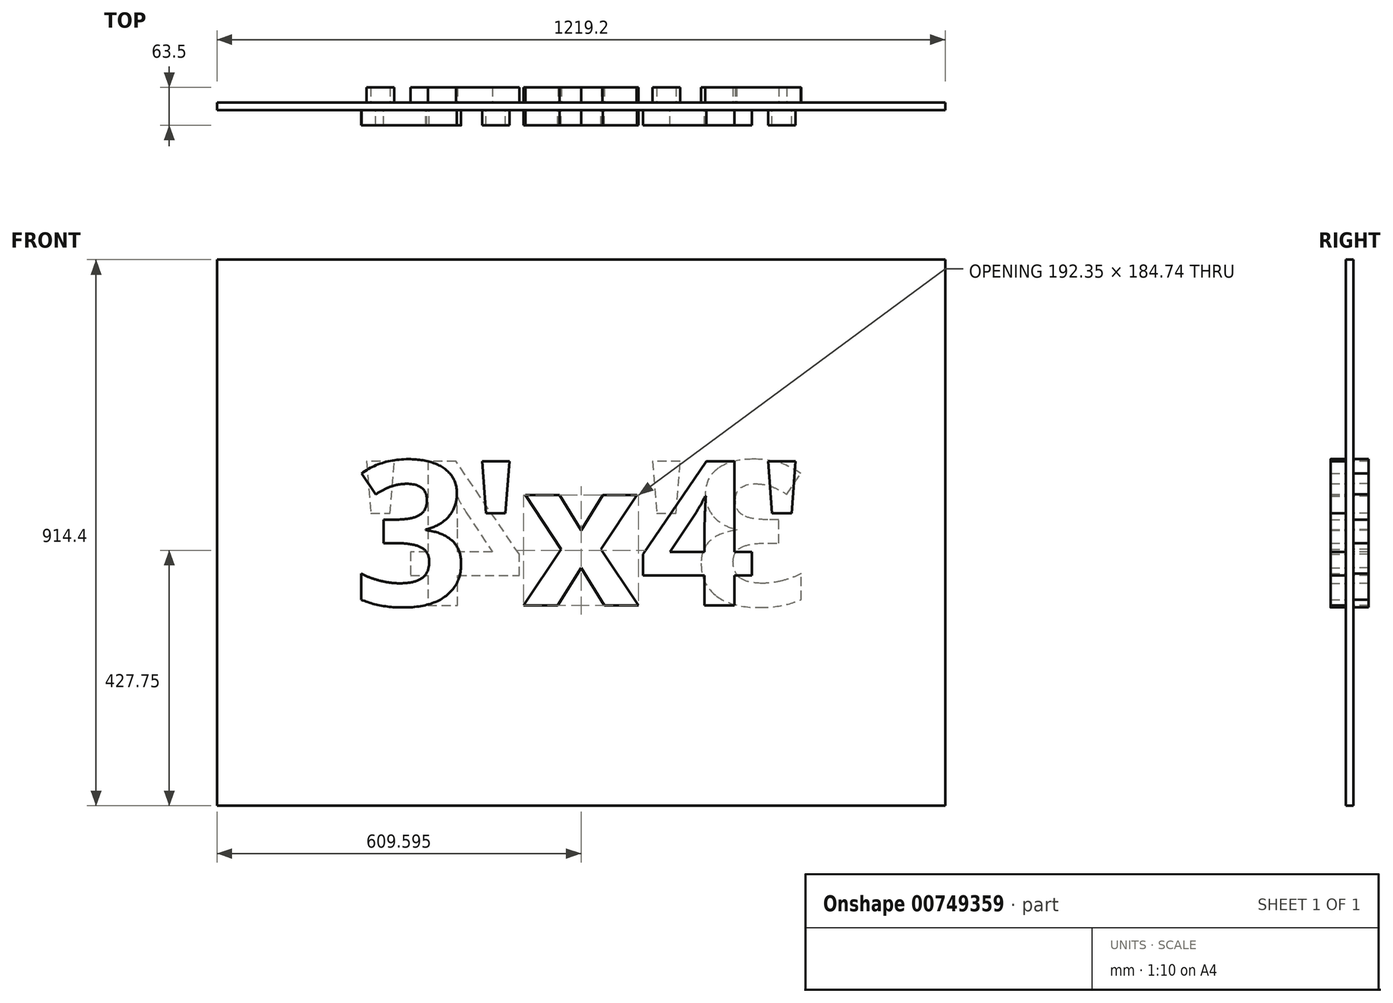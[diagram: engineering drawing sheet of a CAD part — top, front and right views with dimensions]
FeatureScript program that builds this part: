
annotation { "Feature Type Name" : "Feature", "Feature Type Description" : "" }
export const myFeature = defineFeature(function(context is Context, id is Id, definition is map)
    precondition{}
    {
        {
            var Q0;
            Q0=qCreatedBy(makeId("Front.planeOp"),FACE);
            var sketch = newSketch(context, id + "F0", { "sketchPlane" : qUnion([Q0])});
            skLineSegment(sketch, "E0.bottom", {"start": v(0, 0) * mm, "end": v(1219.2, 0) * mm});
            skLineSegment(sketch, "E0.top", {"start": v(0, 914.4) * mm, "end": v(1219.2, 914.4) * mm});
            skLineSegment(sketch, "E0.left", {"start": v(0, 0) * mm, "end": v(0, 914.4) * mm});
            skLineSegment(sketch, "E0.right", {"start": v(1219.2, 0) * mm, "end": v(1219.2, 914.4) * mm});
            skSolve(sketch);
        }
        {
            var Q0;
            Q0=makeQuery(id+"F0.imprint","IMPRINT",FACE,{"disambiguationData":[TD([[makeQuery(id+"F0.imprint","IMPRINT",EDGE,{"derivedFrom":sQuery(id+"F0.wireOp",EDGE,"E0.bottom")}),1.0]])]});
            extrude(context, id + "F1", {"entities" : qUnion([Q0]), "depth" : 12.7 * mm, "offsetDistance" : 25.4 * mm});
        }
        {
            var Q0;
            Q0=makeQuery(id+"F1.opExtrude","CAP_FACE",FACE,{"disambiguationData":[OSD([sQuery(id+"F0.wireOp",EDGE,"E0.bottom"),sQuery(id+"F0.wireOp",EDGE,"E0.top"),sQuery(id+"F0.wireOp",EDGE,"E0.left"),sQuery(id+"F0.wireOp",EDGE,"E0.right")])],"isStart":false});
            var sketch = newSketch(context, id + "F2", { "sketchPlane" : qUnion([Q0])});
            skText(sketch, "E1", { "text": "3\'x4\'", "fontName": "OpenSans-Bold.ttf"});
            skPoint(sketch, "E2", {"position": v(228.6, 457.2) * mm});
            const initialGuessF2  = {"E1": [0.2286, 0.33538, 1, 0, 0.24364]};
            skSetInitialGuess(sketch, initialGuessF2);
            skSolve(sketch);
        }
        {
            var Q0;
            Q0=makeQuery(id+"F2.imprint","IMPRINT",FACE,{"disambiguationData":[TD([[makeQuery(id+"F2.imprint","IMPRINT",EDGE,{"derivedFrom":sQuery(id+"F2.wireOp",EDGE,"E1.sketch_text.stroke-61")}),-1.0]])]});
            var Q1;
            Q1=makeQuery(id+"F2.imprint","IMPRINT",FACE,{"disambiguationData":[TD([[makeQuery(id+"F2.imprint","IMPRINT",EDGE,{"derivedFrom":sQuery(id+"F2.wireOp",EDGE,"E1.sketch_text.stroke-43")}),-1.0]])]});
            var Q2;
            Q2=makeQuery(id+"F2.imprint","IMPRINT",FACE,{"disambiguationData":[TD([[makeQuery(id+"F2.imprint","IMPRINT",EDGE,{"derivedFrom":sQuery(id+"F2.wireOp",EDGE,"E1.sketch_text.stroke-31")}),-1.0]])]});
            var Q3;
            Q3=makeQuery(id+"F2.imprint","IMPRINT",FACE,{"disambiguationData":[TD([[makeQuery(id+"F2.imprint","IMPRINT",EDGE,{"derivedFrom":sQuery(id+"F2.wireOp",EDGE,"E1.sketch_text.stroke-27")}),-1.0]])]});
            var Q4;
            Q4=makeQuery(id+"F2.imprint","IMPRINT",FACE,{"disambiguationData":[TD([[makeQuery(id+"F2.imprint","IMPRINT",EDGE,{"derivedFrom":sQuery(id+"F2.wireOp",EDGE,"E1.sketch_text.stroke-0")}),-1.0]])]});
            extrude(context, id + "F3", {"entities" : qUnion([Q0, Q1, Q2, Q3, Q4]), "operationType" : NewBodyOperationType.ADD, "depth" : 25.4 * mm, "offsetDistance" : 25.4 * mm});
        }
        {
            var Q0;
            Q0=makeQuery(id+"F1.opExtrude","CAP_FACE",FACE,{"disambiguationData":[OSD([sQuery(id+"F0.wireOp",EDGE,"E0.bottom"),sQuery(id+"F0.wireOp",EDGE,"E0.top"),sQuery(id+"F0.wireOp",EDGE,"E0.left"),sQuery(id+"F0.wireOp",EDGE,"E0.right")])],"isStart":true});
            var sketch = newSketch(context, id + "F4", { "sketchPlane" : qUnion([Q0])});
            skText(sketch, "E3", { "text": "3\'x4\'", "fontName": "OpenSans-Bold.ttf"});
            skPoint(sketch, "E4", {"position": v(-990.6, 457.2) * mm});
            const initialGuessF4  = {"E3": [-0.9906, 0.33538, 1, 0, 0.24364]};
            skSetInitialGuess(sketch, initialGuessF4);
            skSolve(sketch);
        }
        {
            var Q0;
            Q0=makeQuery(id+"F4.imprint","IMPRINT",FACE,{"disambiguationData":[TD([[makeQuery(id+"F4.imprint","IMPRINT",EDGE,{"derivedFrom":sQuery(id+"F4.wireOp",EDGE,"E3.sketch_text.stroke-22")}),-1.0]])]});
            var Q1;
            Q1=makeQuery(id+"F4.imprint","IMPRINT",FACE,{"disambiguationData":[TD([[makeQuery(id+"F4.imprint","IMPRINT",EDGE,{"derivedFrom":sQuery(id+"F4.wireOp",EDGE,"E3.sketch_text.stroke-34")}),-1.0]])]});
            var Q2;
            Q2=makeQuery(id+"F4.imprint","IMPRINT",FACE,{"disambiguationData":[TD([[makeQuery(id+"F4.imprint","IMPRINT",EDGE,{"derivedFrom":sQuery(id+"F4.wireOp",EDGE,"E3.sketch_text.stroke-65")}),-1.0]])]});
            var Q3;
            Q3=makeQuery(id+"F4.imprint","IMPRINT",FACE,{"disambiguationData":[TD([[makeQuery(id+"F4.imprint","IMPRINT",EDGE,{"derivedFrom":sQuery(id+"F4.wireOp",EDGE,"E3.sketch_text.stroke-18")}),-1.0]])]});
            var Q4;
            Q4=makeQuery(id+"F4.imprint","IMPRINT",FACE,{"disambiguationData":[TD([[makeQuery(id+"F4.imprint","IMPRINT",EDGE,{"derivedFrom":sQuery(id+"F4.wireOp",EDGE,"E3.sketch_text.stroke-0")}),-1.0]])]});
            var Q5;
            Q5=makeQuery(id+"F4.imprint","IMPRINT",FACE,{"disambiguationData":[TD([[makeQuery(id+"F4.imprint","IMPRINT",EDGE,{"derivedFrom":sQuery(id+"F4.wireOp",EDGE,"E3.sketch_text.stroke-27")}),-1.0]])]});
            var Q6;
            Q6=makeQuery(id+"F4.imprint","IMPRINT",FACE,{"disambiguationData":[TD([[makeQuery(id+"F4.imprint","IMPRINT",EDGE,{"derivedFrom":sQuery(id+"F4.wireOp",EDGE,"E3.sketch_text.stroke-43")}),-1.0]])]});
            var Q7;
            Q7=makeQuery(id+"F4.imprint","IMPRINT",FACE,{"disambiguationData":[TD([[makeQuery(id+"F4.imprint","IMPRINT",EDGE,{"derivedFrom":sQuery(id+"F4.wireOp",EDGE,"E3.sketch_text.stroke-61")}),-1.0]])]});
            extrude(context, id + "F5", {"entities" : qUnion([Q0, Q1, Q2, Q3, Q4, Q5, Q6, Q7]), "operationType" : NewBodyOperationType.ADD, "depth" : 25.4 * mm, "offsetDistance" : 25.4 * mm});
        }
    });
